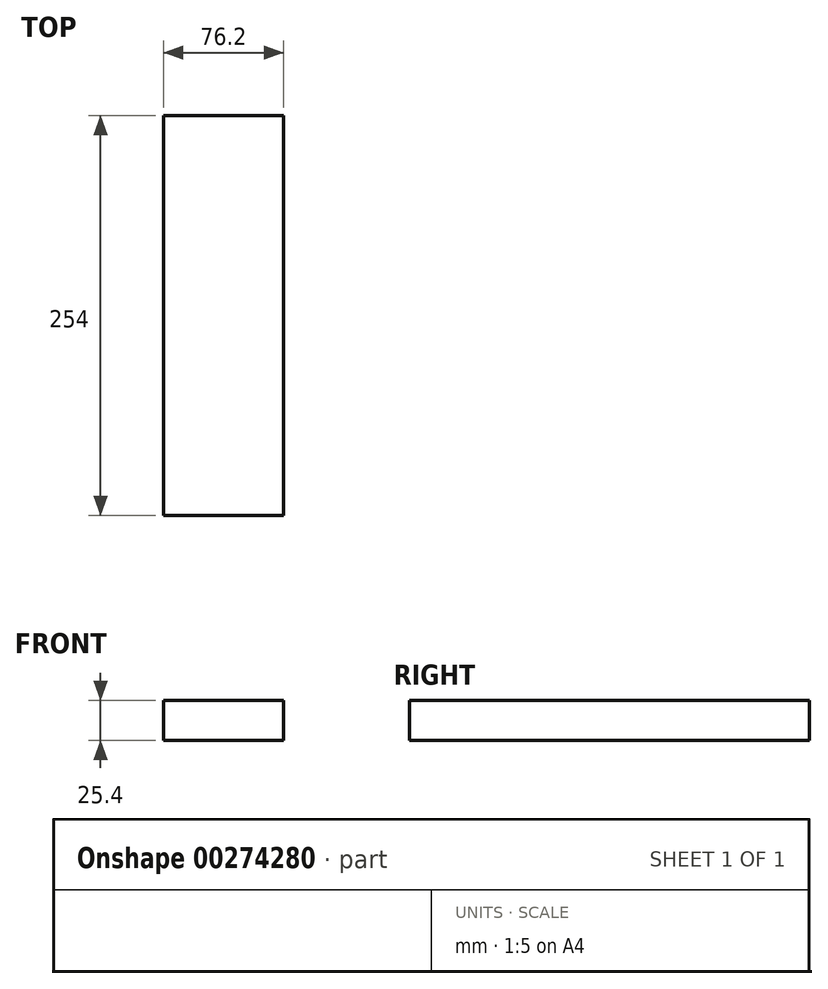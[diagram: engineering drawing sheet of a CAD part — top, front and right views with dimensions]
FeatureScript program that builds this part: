
annotation { "Feature Type Name" : "Feature", "Feature Type Description" : "" }
export const myFeature = defineFeature(function(context is Context, id is Id, definition is map)
    precondition{}
    {
        {
            var Q0;
            Q0=qCreatedBy(makeId("Top.planeOp"),FACE);
            var sketch = newSketch(context, id + "F0", { "sketchPlane" : qUnion([Q0])});
            skLineSegment(sketch, "E0.bottom", {"start": v(-72.83, -117.49) * mm, "end": v(3.37, -117.49) * mm});
            skLineSegment(sketch, "E0.top", {"start": v(-72.83, 136.51) * mm, "end": v(3.37, 136.51) * mm});
            skLineSegment(sketch, "E0.left", {"start": v(-72.83, -117.49) * mm, "end": v(-72.83, 136.51) * mm});
            skLineSegment(sketch, "E0.right", {"start": v(3.37, -117.49) * mm, "end": v(3.37, 136.51) * mm});
            skSolve(sketch);
        }
        {
            var Q0;
            Q0 = qSketchRegion(id + "F0", true);
            extrude(context, id + "F1", {"entities" : qUnion([Q0]), "depth" : 25.4 * mm});
        }
    });
